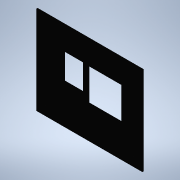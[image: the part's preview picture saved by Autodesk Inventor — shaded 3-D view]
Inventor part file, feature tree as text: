
AUTODESK INVENTOR PART (.ipt)
format: ipt  version: 2022 (Build 260153000, 153)  size: 161,280 bytes
history: native  units: mm
features: reference x21, other x4, sketch x3, hole x2, extrude x1, mirror x1
ambient origin geometry x8: Origin, YZ Plane, XZ Plane, XY Plane, X Axis, Y Axis, Z Axis, Center Point
bodies: Solid1 (feature_tree)
feature tree (32):
  extrude  "Extrusion1"  Depth=6.5mm
  hole  "Hole1"  [1 undecoded]
  mirror  "Mirror1"
  hole  "Hole2"  [1 undecoded]
  sketch  "Sketch1"  dims[d0=6.5mm d1=6.5mm]
  reference  "Reference1"
  reference  "Reference2"
  reference  "Reference3"
  reference  "Reference4"
  reference  "Reference5"
  sketch  "Sketch2"  dims[d2=10.0mm d3=10.0mm]
  sketch  "Sketch3"  dims[d4=10.0mm d5=6.0mm d6=0.0mm d7=17.0mm d8=2.0mm d9=6.0mm d10=4.0mm d11=2.0mm d12=90.0deg d13=8.0mm d14=20.594885mm d15=3.0mm d16=6.0mm d17=4.0mm d18=2.0mm d19=90.0deg d20=8.0mm d21=20.594885mm]
  reference  "Reference6"
  reference  "Reference7"
  reference  "Reference8"
  reference  "Reference9"
  reference  "Reference10"
  reference  "Reference11"
  reference  "Reference12"
  reference  "Reference13"
  reference  "Reference14"
  reference  "Reference15"
  reference  "Reference16"
  reference  "Reference17"
  reference  "Reference18"
  reference  "Reference19"
  reference  "Reference20"
  reference  "Reference21"
  other  "<userpath>\Documents\Inventor\etchasketch\etchasketch.iam"
  other  "etchasketch.iam"
  other  "lag3:1"
  other  "skærm:1"
note: 2 required parameter values undecoded (feature->parameter linkage not recoverable at this tier; creation-order binding heuristic only, values carry confidence <= 0.55)
